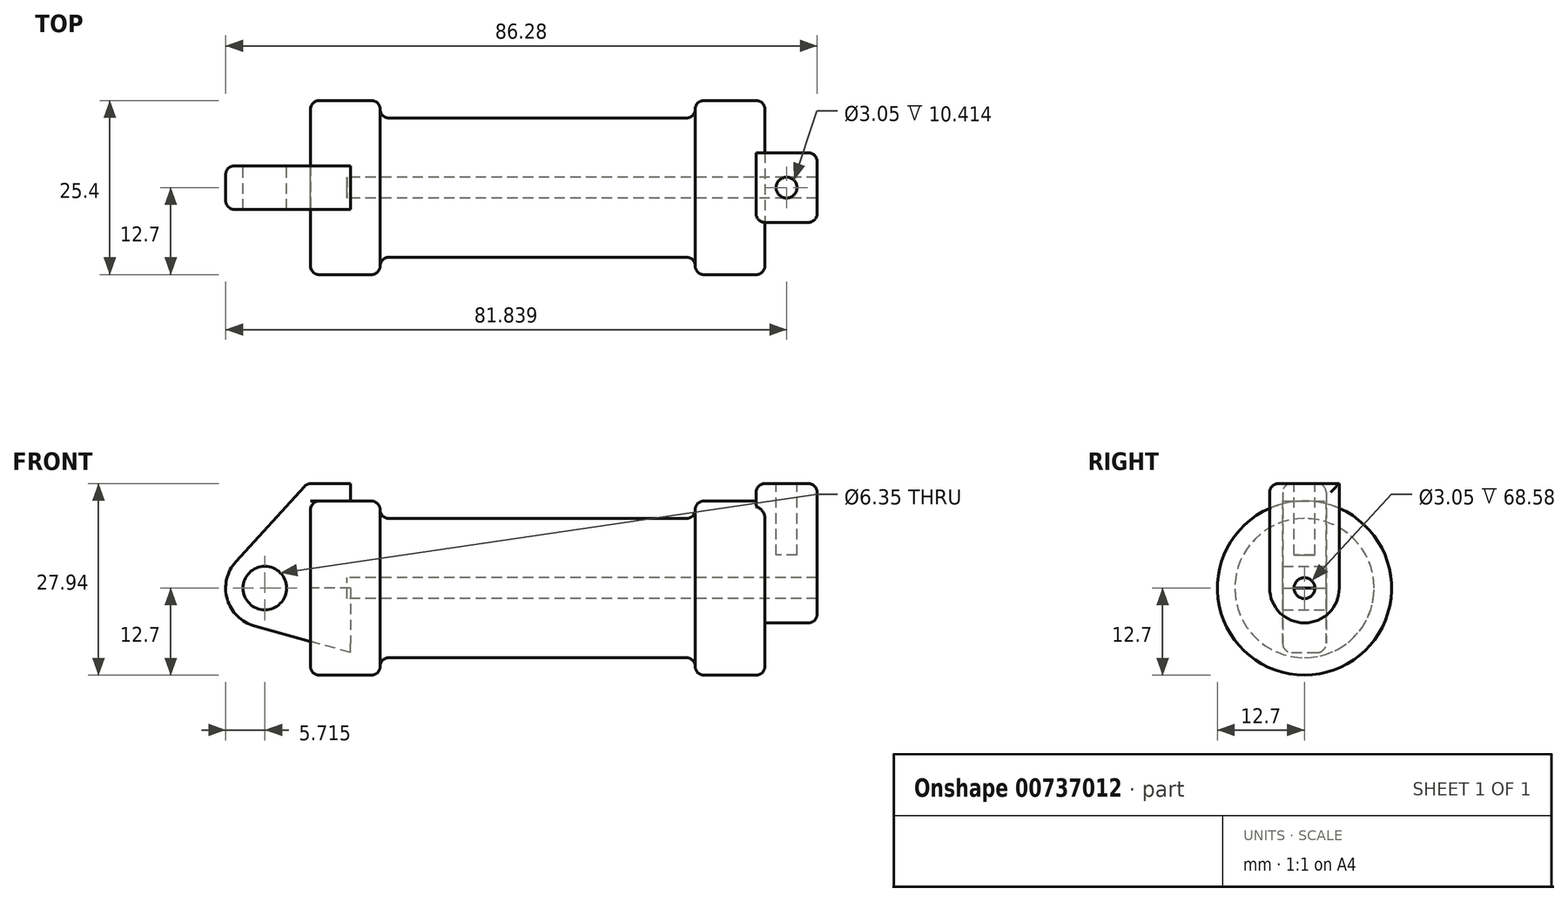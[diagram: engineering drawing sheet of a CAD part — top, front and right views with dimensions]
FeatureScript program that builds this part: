
annotation { "Feature Type Name" : "Feature", "Feature Type Description" : "" }
export const myFeature = defineFeature(function(context is Context, id is Id, definition is map)
    precondition{}
    {
        {
            var Q0;
            Q0=qCreatedBy(makeId("Front.planeOp"),FACE);
            var sketch = newSketch(context, id + "F0", { "sketchPlane" : qUnion([Q0])});
            skLineSegment(sketch, "E0", {"start": v(0, 0) * mm, "end": v(0, 12.7) * mm});
            skLineSegment(sketch, "E1", {"start": v(0, 12.7) * mm, "end": v(10.16, 12.7) * mm});
            skLineSegment(sketch, "E2", {"start": v(10.16, 12.7) * mm, "end": v(10.16, 10.16) * mm});
            skLineSegment(sketch, "E3", {"start": v(10.16, 10.16) * mm, "end": v(56.13, 10.16) * mm});
            skLineSegment(sketch, "E4", {"start": v(56.13, 10.16) * mm, "end": v(56.13, 12.7) * mm});
            skLineSegment(sketch, "E5", {"start": v(56.13, 12.7) * mm, "end": v(66.3, 12.7) * mm});
            skLineSegment(sketch, "E6", {"start": v(66.3, 12.7) * mm, "end": v(66.3, 0) * mm});
            skLineSegment(sketch, "E7", {"start": v(66.3, 0) * mm, "end": v(0, 0) * mm});
            skLineSegment(sketch, "E8", {"start": v(5.84, 15.24) * mm, "end": v(-0.5, 15.24) * mm});
            skLineSegment(sketch, "E9", {"start": v(-0.5, 15.24) * mm, "end": v(-10.88, 3.85) * mm});
            skLineSegment(sketch, "E10", {"start": v(0, 0) * mm, "end": v(-6.65, 0) * mm});
            skCircle(sketch, "E11", {"center": v(-6.65, 0) * mm, "radius": 5.72 * mm});
            skCircle(sketch, "E12", {"center": v(-6.65, 0) * mm, "radius": 3.18 * mm});
            skLineSegment(sketch, "E13", {"start": v(5.84, 15.24) * mm, "end": v(5.84, -9.4) * mm});
            skLineSegment(sketch, "E14", {"start": v(5.84, -9.4) * mm, "end": v(-8.18, -5.5) * mm});
            skSolve(sketch);
        }
        {
            var Q0;
            {var subQ0=sQuery(id+"F0.wireOp",EDGE,"E2");Q0=makeQuery(id+"F0.imprint","IMPRINT",FACE,{"disambiguationData":[TD([[makeQuery(id+"F0.imprint","IMPRINT",EDGE,{"derivedFrom":subQ0}),-1.0]])]});}
            var Q1;
            {var subQ0=sQuery(id+"F0.wireOp",EDGE,"E0");Q1=makeQuery(id+"F0.imprint","IMPRINT",FACE,{"disambiguationData":[TD([[makeQuery(id+"F0.imprint","IMPRINT",EDGE,{"derivedFrom":subQ0}),-1.0]])]});}
            var Q2;
            Q2=sQuery(id+"F0.wireOp",EDGE,"E7");
            revolve(context, id + "F1", {"surfaceOperationType" : NewSurfaceOperationType.NEW, "entities" : qUnion([Q0, Q1]), "axis" : qUnion([Q2]), "revolveType" : RevolveType.FULL});
        }
        {
            var Q0;
            Q0=makeQuery(id+"F1.opRevolve","SWEPT_FACE",FACE,{"disambiguationData":[OSD([sQuery(id+"F0.wireOp",EDGE,"E6")])]});
            var sketch = newSketch(context, id + "F2", { "sketchPlane" : qUnion([Q0])});
            skCircle(sketch, "E15", {"center": v(0, 0) * mm, "radius": 1.52 * mm});
            skCircle(sketch, "E16", {"center": v(0, 0) * mm, "radius": 5.08 * mm});
            skLineSegment(sketch, "E17", {"start": v(-5.08, 0) * mm, "end": v(-5.08, 15.24) * mm});
            skLineSegment(sketch, "E18", {"start": v(-5.08, 15.24) * mm, "end": v(5.08, 15.24) * mm});
            skLineSegment(sketch, "E19", {"start": v(5.08, 15.24) * mm, "end": v(5.08, 0) * mm});
            skSolve(sketch);
        }
        {
            var Q0;
            {var subQ0=sQuery(id+"F2.wireOp",EDGE,"E18");Q0=makeQuery(id+"F2.imprint","IMPRINT",FACE,{"disambiguationData":[TD([[makeQuery(id+"F2.imprint","IMPRINT",EDGE,{"derivedFrom":subQ0}),-1.0]])]});}
            var Q1;
            {var subQ0=sQuery(id+"F2.wireOp",EDGE,"E17");var subQ1=sQuery(id+"F2.wireOp",EDGE,"E16");var subQ2=makeQuery(id+"F2.imprint","INTERSECT",VERTEX,{"derivedFrom":[subQ1,subQ0]});Q1=makeQuery(id+"F2.imprint","IMPRINT",FACE,{"disambiguationData":[TD([[makeQuery(id+"F2.imprint","IMPRINT",EDGE,{"disambiguationData":[TD([[subQ2,1.0]])],"derivedFrom":subQ1}),-1.0]])]});}
            var Q2;
            Q2=makeQuery(id+"F2.imprint","IMPRINT",FACE,{"disambiguationData":[TD([[makeQuery(id+"F2.imprint","IMPRINT",EDGE,{"derivedFrom":sQuery(id+"F2.wireOp",EDGE,"E15")}),-1.0]])]});
            extrude(context, id + "F3", {"entities" : qUnion([Q0, Q1, Q2]), "operationType" : NewBodyOperationType.ADD, "depth" : 7.62 * mm, "offsetDistance" : 25.4 * mm});
        }
        {
            var Q0;
            Q0 = qSketchRegion(id + "F2", true);
            extrude(context, id + "F4", {"entities" : qUnion([Q0]), "operationType" : NewBodyOperationType.ADD, "oppositeDirection" : true, "depth" : 1.27 * mm, "offsetDistance" : 25.4 * mm});
        }
        {
            var Q0;
            Q0=makeQuery(id+"F2.imprint","IMPRINT",FACE,{"disambiguationData":[TD([[makeQuery(id+"F2.imprint","IMPRINT",EDGE,{"derivedFrom":sQuery(id+"F2.wireOp",EDGE,"E15")}),1.0]])]});
            extrude(context, id + "F5", {"entities" : qUnion([Q0]), "operationType" : NewBodyOperationType.REMOVE, "oppositeDirection" : true, "depth" : 60.96 * mm, "offsetDistance" : 25.4 * mm});
        }
        {
            var Q0;
            {var subQ0=sQuery(id+"F2.wireOp",EDGE,"E18");Q0=makeQuery(id+"F4.boolean.opBoolean","MERGE",FACE,{"derivedFrom":[makeQuery(id+"F3.opExtrude","SWEPT_FACE",FACE,{"disambiguationData":[OSD([subQ0])]}),makeQuery(id+"F4.opExtrude","SWEPT_FACE",FACE,{"disambiguationData":[OSD([subQ0])]})]});}
            var sketch = newSketch(context, id + "F6", { "sketchPlane" : qUnion([Q0])});
            skLineSegment(sketch, "E20", {"start": v(65.02, 0) * mm, "end": v(73.91, 0) * mm});
            skCircle(sketch, "E21", {"center": v(69.47, 0) * mm, "radius": 1.52 * mm});
            skSolve(sketch);
        }
        {
            var Q0;
            {var subQ0=sQuery(id+"F6.wireOp",EDGE,"E21");var subQ1=sQuery(id+"F6.wireOp",EDGE,"E20");var subQ2=makeQuery(id+"F6.imprint","INTERSECT",VERTEX,{"disambiguationData":[OD(0.0)],"derivedFrom":[subQ1,subQ0]});Q0=makeQuery(id+"F6.imprint","IMPRINT",FACE,{"disambiguationData":[TD([[makeQuery(id+"F6.imprint","IMPRINT",EDGE,{"disambiguationData":[TD([[subQ2,-1.0]])],"derivedFrom":subQ1}),1.0]])]});}
            var Q1;
            {var subQ0=sQuery(id+"F6.wireOp",EDGE,"E21");var subQ1=sQuery(id+"F6.wireOp",EDGE,"E20");var subQ2=makeQuery(id+"F6.imprint","INTERSECT",VERTEX,{"disambiguationData":[OD(0.0)],"derivedFrom":[subQ1,subQ0]});Q1=makeQuery(id+"F6.imprint","IMPRINT",FACE,{"disambiguationData":[TD([[makeQuery(id+"F6.imprint","IMPRINT",EDGE,{"disambiguationData":[TD([[subQ2,-1.0]])],"derivedFrom":subQ1}),-1.0]])]});}
            var Q2;
            Q2=sQuery(id+"F6.wireOp",EDGE,"E21");
            extrude(context, id + "F7", {"entities" : qUnion([Q0, Q1]), "operationType" : NewBodyOperationType.REMOVE, "surfaceEntities" : qUnion([Q2]), "oppositeDirection" : true, "depth" : 10.4 * mm, "offsetDistance" : 25.4 * mm});
        }
        {
            var Q0;
            Q0=makeQuery(id+"F1.opRevolve","SWEPT_EDGE",EDGE,{"disambiguationData":[OSD([sQuery(id+"F0.wireOp",EDGE,"E1"),sQuery(id+"F0.wireOp",EDGE,"E2")])]});
            fillet(context, id + "F8", {"entities" : qUnion([Q0]), "radius" : 1.27 * mm, "tangentPropagation" : true, "allowEdgeOverflow" : false});
        }
        {
            var Q0;
            Q0=makeQuery(id+"F1.opRevolve","SWEPT_EDGE",EDGE,{"disambiguationData":[OSD([sQuery(id+"F0.wireOp",EDGE,"E4"),sQuery(id+"F0.wireOp",EDGE,"E5")])]});
            fillet(context, id + "F9", {"entities" : qUnion([Q0]), "radius" : 1.27 * mm, "tangentPropagation" : true, "allowEdgeOverflow" : false});
        }
        {
            var Q0;
            Q0=makeQuery(id+"F1.opRevolve","SWEPT_EDGE",EDGE,{"disambiguationData":[OSD([sQuery(id+"F0.wireOp",EDGE,"E2"),sQuery(id+"F0.wireOp",EDGE,"E3")])]});
            fillet(context, id + "F10", {"entities" : qUnion([Q0]), "radius" : 1.27 * mm, "tangentPropagation" : true, "allowEdgeOverflow" : false});
        }
        {
            var Q0;
            Q0=makeQuery(id+"F1.opRevolve","SWEPT_EDGE",EDGE,{"disambiguationData":[OSD([sQuery(id+"F0.wireOp",EDGE,"E3"),sQuery(id+"F0.wireOp",EDGE,"E4")])]});
            fillet(context, id + "F11", {"entities" : qUnion([Q0]), "radius" : 1.27 * mm, "tangentPropagation" : true, "allowEdgeOverflow" : false});
        }
        {
            var Q0;
            Q0=makeQuery(id+"F1.opRevolve","SWEPT_EDGE",EDGE,{"disambiguationData":[OSD([sQuery(id+"F0.wireOp",EDGE,"E0"),sQuery(id+"F0.wireOp",EDGE,"E1")])]});
            fillet(context, id + "F12", {"entities" : qUnion([Q0]), "radius" : 1.27 * mm, "tangentPropagation" : true, "allowEdgeOverflow" : false});
        }
        {
            var Q0;
            {var subQ0=sQuery(id+"F0.wireOp",EDGE,"E5");var subQ1=sQuery(id+"F0.wireOp",EDGE,"E6");Q0=makeQuery(id+"F3.boolean.opBoolean","SPLIT",EDGE,{"disambiguationData":[topologyDisambiguationEdgeConnected([makeQuery(id+"F1.opRevolve","SWEPT_FACE",FACE,{"disambiguationData":[OSD([subQ1])]})])],"derivedFrom":makeQuery(id+"F1.opRevolve","SWEPT_EDGE",EDGE,{"disambiguationData":[OSD([subQ0,subQ1])]})});}
            fillet(context, id + "F13", {"entities" : qUnion([Q0]), "radius" : 1.27 * mm, "tangentPropagation" : true, "allowEdgeOverflow" : false});
        }
        {
            var Q0;
            {var subQ1=sQuery(id+"F0.wireOp",EDGE,"E0");Q0=makeQuery(id+"F0.imprint","IMPRINT",FACE,{"disambiguationData":[TD([[makeQuery(id+"F0.imprint","IMPRINT",EDGE,{"derivedFrom":subQ1}),1.0]])]});}
            var Q1;
            {var subQ0=sQuery(id+"F0.wireOp",EDGE,"E14");Q1=makeQuery(id+"F0.imprint","IMPRINT",FACE,{"disambiguationData":[TD([[makeQuery(id+"F0.imprint","IMPRINT",EDGE,{"derivedFrom":subQ0}),-1.0]])]});}
            var Q2;
            {var subQ5=sQuery(id+"F0.wireOp",EDGE,"E12");Q2=makeQuery(id+"F0.imprint","IMPRINT",FACE,{"disambiguationData":[TD([[makeQuery(id+"F0.imprint","IMPRINT",EDGE,{"derivedFrom":subQ5}),-1.0]])]});}
            extrude(context, id + "F14", {"entities" : qUnion([Q0, Q1, Q2]), "endBound" : BoundingType.SYMMETRIC, "depth" : 6.35 * mm, "offsetDistance" : 25.4 * mm});
        }
        {
            var Q0;
            Q0=makeQuery(id+"F14.opExtrude","SWEPT_EDGE",EDGE,{"disambiguationData":[OSD([sQuery(id+"F0.wireOp",EDGE,"E8"),sQuery(id+"F0.wireOp",EDGE,"E9")])]});
            fillet(context, id + "F15", {"entities" : qUnion([Q0]), "radius" : 1.27 * mm, "tangentPropagation" : true, "allowEdgeOverflow" : false});
        }
        {
            var Q0;
            Q0=makeQuery(id+"F14.opExtrude","CAP_EDGE",EDGE,{"disambiguationData":[OSD([sQuery(id+"F0.wireOp",EDGE,"E8")])],"isStart":false});
            fillet(context, id + "F16", {"entities" : qUnion([Q0]), "radius" : 1.27 * mm, "tangentPropagation" : true, "allowEdgeOverflow" : false});
        }
        {
            var Q0;
            Q0=makeQuery(id+"F14.opExtrude","CAP_EDGE",EDGE,{"disambiguationData":[OSD([sQuery(id+"F0.wireOp",EDGE,"E8")])],"isStart":true});
            fillet(context, id + "F17", {"entities" : qUnion([Q0]), "radius" : 1.27 * mm, "tangentPropagation" : true, "allowEdgeOverflow" : false});
        }
        {
            var Q0;
            Q0=makeQuery(id+"F4.opExtrude","CAP_EDGE",EDGE,{"disambiguationData":[OSD([sQuery(id+"F2.wireOp",EDGE,"E18")])],"isStart":false});
            fillet(context, id + "F18", {"entities" : qUnion([Q0]), "radius" : 1.27 * mm, "tangentPropagation" : true, "allowEdgeOverflow" : false});
        }
        {
            var Q0;
            {var subQ0=sQuery(id+"F2.wireOp",EDGE,"E18");var subQ1=sQuery(id+"F2.wireOp",EDGE,"E17");Q0=makeQuery(id+"F4.boolean.opBoolean","MERGE",EDGE,{"derivedFrom":[makeQuery(id+"F3.opExtrude","SWEPT_EDGE",EDGE,{"disambiguationData":[OSD([subQ1,subQ0])]}),makeQuery(id+"F4.opExtrude","SWEPT_EDGE",EDGE,{"disambiguationData":[OSD([subQ1,subQ0])]})]});}
            fillet(context, id + "F19", {"entities" : qUnion([Q0]), "radius" : 1.27 * mm, "tangentPropagation" : true, "allowEdgeOverflow" : false});
        }
        {
            var Q0;
            Q0=makeQuery(id+"F3.opExtrude","CAP_EDGE",EDGE,{"disambiguationData":[OSD([sQuery(id+"F2.wireOp",EDGE,"E17")])],"isStart":false});
            fillet(context, id + "F20", {"entities" : qUnion([Q0]), "radius" : 1.27 * mm, "tangentPropagation" : true, "allowEdgeOverflow" : false});
        }
    });
